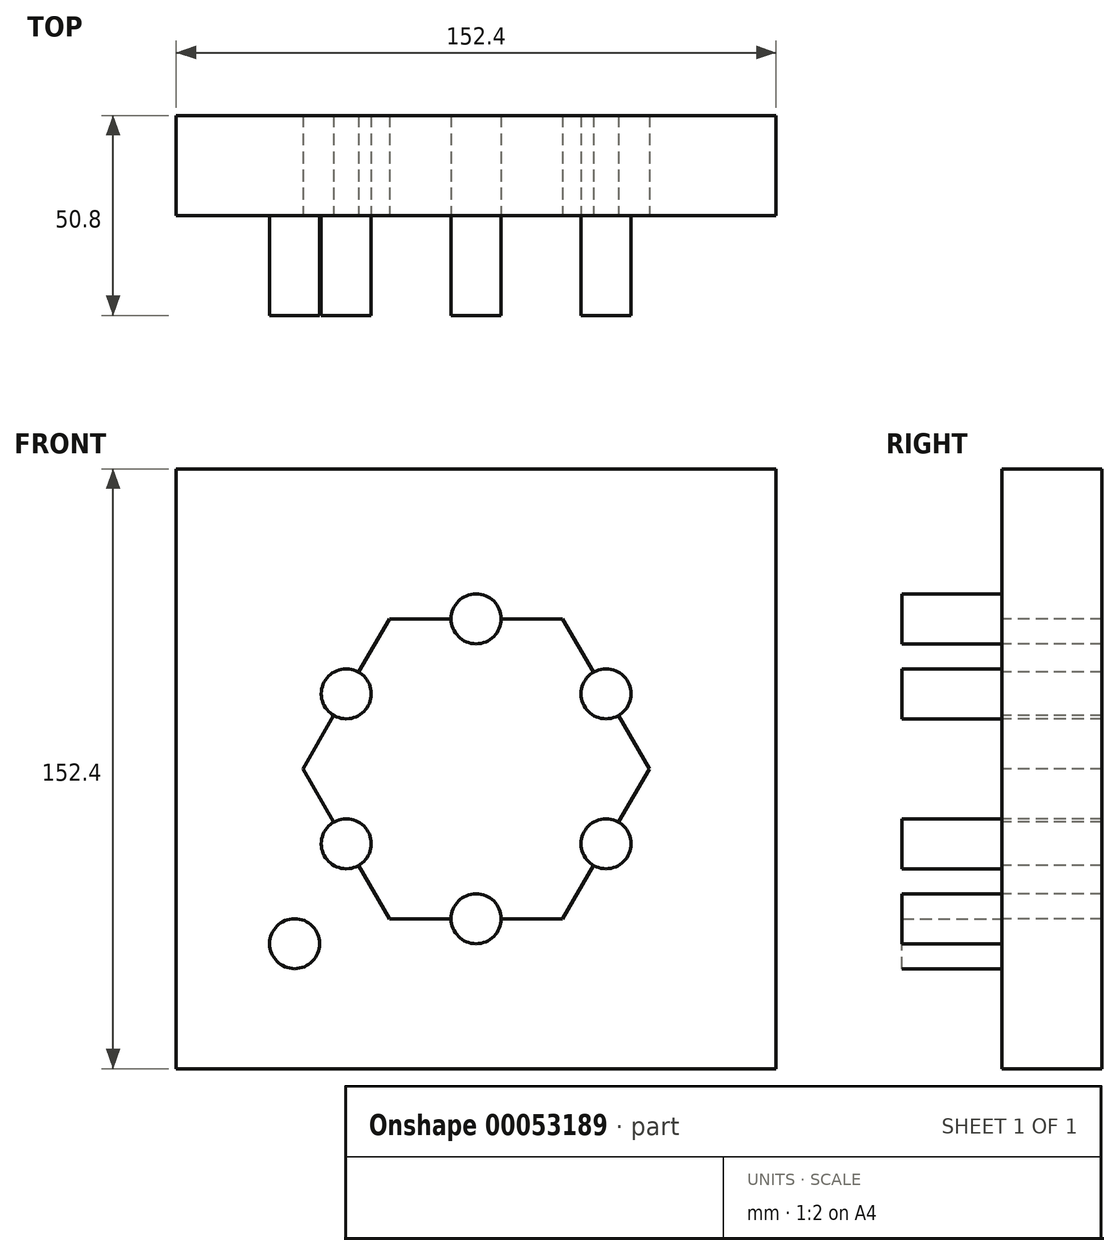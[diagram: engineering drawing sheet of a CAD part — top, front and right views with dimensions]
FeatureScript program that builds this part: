
annotation { "Feature Type Name" : "Feature", "Feature Type Description" : "" }
export const myFeature = defineFeature(function(context is Context, id is Id, definition is map)
    precondition{}
    {
        {
            var Q0;
            Q0=qCreatedBy(makeId("Front.planeOp"),FACE);
            var sketch = newSketch(context, id + "F0", { "sketchPlane" : qUnion([Q0])});
            skLineSegment(sketch, "E0.rect.bottom", {"start": v(76.2, 76.2) * mm, "end": v(-76.2, 76.2) * mm});
            skLineSegment(sketch, "E0.rect.top", {"start": v(76.2, -76.2) * mm, "end": v(-76.2, -76.2) * mm});
            skLineSegment(sketch, "E0.rect.left", {"start": v(76.2, 76.2) * mm, "end": v(76.2, -76.2) * mm});
            skLineSegment(sketch, "E0.rect.right", {"start": v(-76.2, 76.2) * mm, "end": v(-76.2, -76.2) * mm});
            skPoint(sketch, "E0.rect.middle", {"position": v(0, 0) * mm});
            skPoint(sketch, "E1.0.midPoint", {"position": v(33, 0) * mm});
            skCircle(sketch, "E2", {"center": v(0, 38.1) * mm, "radius": 6.35 * mm});
            skCircle(sketch, "E3", {"center": v(-33, 19.05) * mm, "radius": 6.35 * mm});
            skCircle(sketch, "E4", {"center": v(-33, -19.05) * mm, "radius": 6.35 * mm});
            skCircle(sketch, "E5", {"center": v(0, -38.1) * mm, "radius": 6.35 * mm});
            skCircle(sketch, "E6", {"center": v(33, -19.05) * mm, "radius": 6.35 * mm});
            skCircle(sketch, "E7", {"center": v(33, 19.05) * mm, "radius": 6.35 * mm});
            skLineSegment(sketch, "E8", {"start": v(-33, -19.05) * mm, "end": v(-46.11, -44.44) * mm, "construction": true});
            skCircle(sketch, "E9", {"center": v(-46.11, -44.44) * mm, "radius": 6.35 * mm});
            skCircle(sketch, "E10.cCircle", {"center": v(0, 0) * mm, "radius": 38.1 * mm, "construction": true});
            skLineSegment(sketch, "E10.0", {"start": v(22, 38.1) * mm, "end": v(44, 0) * mm});
            skLineSegment(sketch, "E10.1", {"start": v(44, 0) * mm, "end": v(22, -38.1) * mm});
            skLineSegment(sketch, "E10.2", {"start": v(22, -38.1) * mm, "end": v(-22, -38.1) * mm});
            skLineSegment(sketch, "E10.3", {"start": v(-22, -38.1) * mm, "end": v(-44, 0) * mm});
            skLineSegment(sketch, "E10.4", {"start": v(-44, 0) * mm, "end": v(-22, 38.1) * mm});
            skLineSegment(sketch, "E10.5", {"start": v(-22, 38.1) * mm, "end": v(22, 38.1) * mm});
            skSolve(sketch);
        }
        {
            var Q0;
            Q0=makeQuery(id+"F0.imprint","IMPRINT",FACE,{"disambiguationData":[TD([[makeQuery(id+"F0.imprint","IMPRINT",EDGE,{"derivedFrom":sQuery(id+"F0.wireOp",EDGE,"E0.rect.bottom")}),1.0]])]});
            var Q1;
            Q1=makeQuery(id+"F0.imprint","IMPRINT",FACE,{"disambiguationData":[TD([[makeQuery(id+"F0.imprint","IMPRINT",EDGE,{"derivedFrom":sQuery(id+"F0.wireOp",EDGE,"E4")}),1.0]])]});
            var Q2;
            Q2=makeQuery(id+"F0.imprint","IMPRINT",FACE,{"disambiguationData":[TD([[makeQuery(id+"F0.imprint","IMPRINT",EDGE,{"derivedFrom":sQuery(id+"F0.wireOp",EDGE,"E3")}),1.0]])]});
            var Q3;
            Q3=makeQuery(id+"F0.imprint","IMPRINT",FACE,{"disambiguationData":[TD([[makeQuery(id+"F0.imprint","IMPRINT",EDGE,{"derivedFrom":sQuery(id+"F0.wireOp",EDGE,"E2")}),1.0]])]});
            var Q4;
            Q4=makeQuery(id+"F0.imprint","IMPRINT",FACE,{"disambiguationData":[TD([[makeQuery(id+"F0.imprint","IMPRINT",EDGE,{"derivedFrom":sQuery(id+"F0.wireOp",EDGE,"E7")}),1.0]])]});
            var Q5;
            Q5=makeQuery(id+"F0.imprint","IMPRINT",FACE,{"disambiguationData":[TD([[makeQuery(id+"F0.imprint","IMPRINT",EDGE,{"derivedFrom":sQuery(id+"F0.wireOp",EDGE,"E6")}),1.0]])]});
            var Q6;
            Q6=makeQuery(id+"F0.imprint","IMPRINT",FACE,{"disambiguationData":[TD([[makeQuery(id+"F0.imprint","IMPRINT",EDGE,{"derivedFrom":sQuery(id+"F0.wireOp",EDGE,"E5")}),1.0]])]});
            var Q7;
            Q7=makeQuery(id+"F0.imprint","IMPRINT",FACE,{"disambiguationData":[TD([[makeQuery(id+"F0.imprint","IMPRINT",EDGE,{"derivedFrom":sQuery(id+"F0.wireOp",EDGE,"E9")}),1.0]])]});
            extrude(context, id + "F1", {"entities" : qUnion([Q0, Q1, Q2, Q3, Q4, Q5, Q6, Q7]), "oppositeDirection" : true, "depth" : 25.4 * mm});
        }
        {
            var Q0;
            Q0=makeQuery(id+"F0.imprint","IMPRINT",FACE,{"disambiguationData":[TD([[makeQuery(id+"F0.imprint","IMPRINT",EDGE,{"derivedFrom":sQuery(id+"F0.wireOp",EDGE,"E3")}),1.0]])]});
            var Q1;
            Q1=makeQuery(id+"F0.imprint","IMPRINT",FACE,{"disambiguationData":[TD([[makeQuery(id+"F0.imprint","IMPRINT",EDGE,{"derivedFrom":sQuery(id+"F0.wireOp",EDGE,"E4")}),1.0]])]});
            var Q2;
            Q2=makeQuery(id+"F0.imprint","IMPRINT",FACE,{"disambiguationData":[TD([[makeQuery(id+"F0.imprint","IMPRINT",EDGE,{"derivedFrom":sQuery(id+"F0.wireOp",EDGE,"E5")}),1.0]])]});
            var Q3;
            Q3=makeQuery(id+"F0.imprint","IMPRINT",FACE,{"disambiguationData":[TD([[makeQuery(id+"F0.imprint","IMPRINT",EDGE,{"derivedFrom":sQuery(id+"F0.wireOp",EDGE,"E7")}),1.0]])]});
            var Q4;
            Q4=makeQuery(id+"F0.imprint","IMPRINT",FACE,{"disambiguationData":[TD([[makeQuery(id+"F0.imprint","IMPRINT",EDGE,{"derivedFrom":sQuery(id+"F0.wireOp",EDGE,"E6")}),1.0]])]});
            var Q5;
            Q5=makeQuery(id+"F0.imprint","IMPRINT",FACE,{"disambiguationData":[TD([[makeQuery(id+"F0.imprint","IMPRINT",EDGE,{"derivedFrom":sQuery(id+"F0.wireOp",EDGE,"E2")}),1.0]])]});
            var Q6;
            Q6=makeQuery(id+"F0.imprint","IMPRINT",FACE,{"disambiguationData":[TD([[makeQuery(id+"F0.imprint","IMPRINT",EDGE,{"derivedFrom":sQuery(id+"F0.wireOp",EDGE,"E9")}),1.0]])]});
            extrude(context, id + "F2", {"entities" : qUnion([Q0, Q1, Q2, Q3, Q4, Q5, Q6]), "operationType" : NewBodyOperationType.ADD, "depth" : 25.4 * mm});
        }
    });
